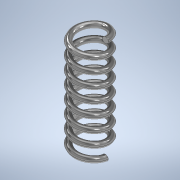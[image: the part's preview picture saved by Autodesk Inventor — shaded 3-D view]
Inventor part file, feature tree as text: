
AUTODESK INVENTOR PART (.ipt)
format: ipt  version: 2021 (Build 250183000, 183)  size: 217,600 bytes
history: native  units: mm
features: other x1, sketch x1
ambient origin geometry x8: Origin, YZ Plane, XZ Plane, XY Plane, X Axis, Y Axis, Z Axis, Center Point
bodies: Body1 (feature_tree)
feature tree (2):
  other  "Espiral1"
  sketch  "Esboço1"  dims[d3=0.08mm d4=0.21mm d5=0.5mm d6=1.395mm d7=80.0mm d8=0.0mm d9=90.0deg d10=90.0deg d11=0.0mm d12=0.0mm]
